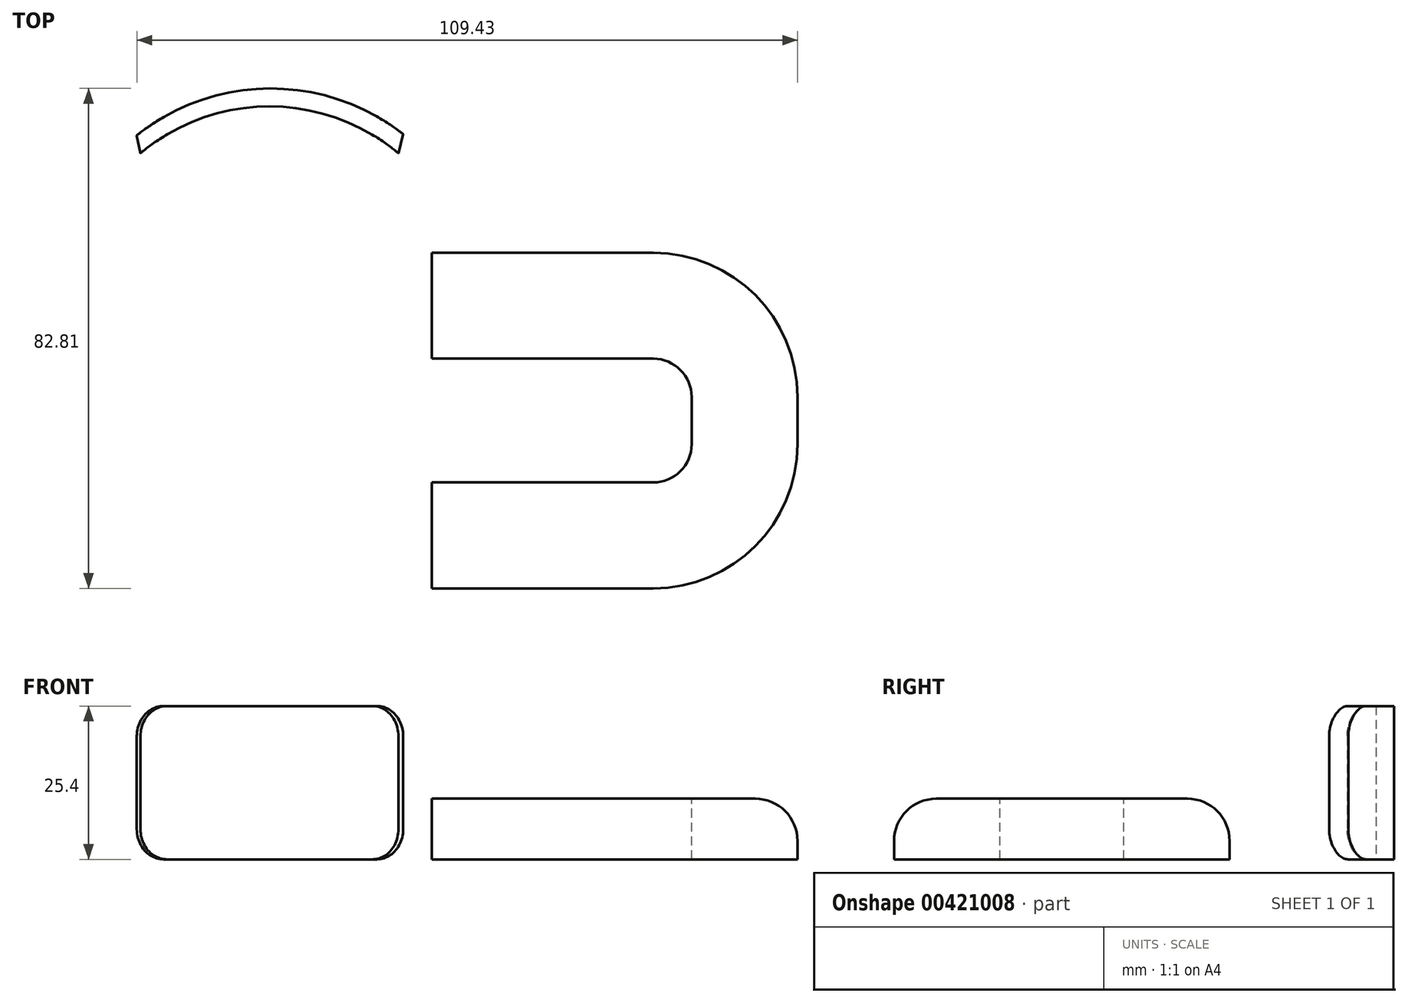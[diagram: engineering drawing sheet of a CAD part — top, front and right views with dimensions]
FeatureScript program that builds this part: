
annotation { "Feature Type Name" : "Feature", "Feature Type Description" : "" }
export const myFeature = defineFeature(function(context is Context, id is Id, definition is map)
    precondition{}
    {
        {
            var Q0;
            Q0=qCreatedBy(makeId("Right.planeOp"),FACE);
            var sketch = newSketch(context, id + "F0", { "sketchPlane" : qUnion([Q0])});
            skLineSegment(sketch, "E0.bottom", {"start": v(0, 0) * mm, "end": v(17.54, 0) * mm});
            skLineSegment(sketch, "E0.top", {"start": v(0, 10.05) * mm, "end": v(10.54, 10.05) * mm});
            skLineSegment(sketch, "E0.left", {"start": v(0, 0) * mm, "end": v(0, 10.05) * mm});
            skLineSegment(sketch, "E0.right", {"start": v(17.54, 0) * mm, "end": v(17.54, 3.05) * mm});
            skPoint(sketch, "E1.visualSharp", {"position": v(17.54, 10.05) * mm});
            skArc(sketch, "E1.filletArc", {"start": v(17.54, 3.05) * mm, "mid": v(15.49, 8) * mm, "end": v(10.54, 10.05) * mm});
            skSolve(sketch);
        }
        {
            var Q0;
            Q0=qCreatedBy(makeId("Top.planeOp"),FACE);
            var sketch = newSketch(context, id + "F1", { "sketchPlane" : qUnion([Q0])});
            skLineSegment(sketch, "E2", {"start": v(0, 0) * mm, "end": v(36.67, 0) * mm});
            skLineSegment(sketch, "E3", {"start": v(43.02, -6.35) * mm, "end": v(43.02, -14.16) * mm});
            skLineSegment(sketch, "E4", {"start": v(36.67, -20.5) * mm, "end": v(0, -20.5) * mm});
            skPoint(sketch, "E5.visualSharp", {"position": v(43.02, 0) * mm});
            skArc(sketch, "E5.filletArc", {"start": v(43.02, -6.35) * mm, "mid": v(41.16, -1.86) * mm, "end": v(36.67, 0) * mm});
            skPoint(sketch, "E6.visualSharp", {"position": v(43.02, -20.5) * mm});
            skArc(sketch, "E6.filletArc", {"start": v(36.67, -20.5) * mm, "mid": v(41.16, -18.65) * mm, "end": v(43.02, -14.16) * mm});
            skSolve(sketch);
        }
        {
            var Q0;
            Q0=makeQuery(id+"F0.imprint","IMPRINT",FACE,{"disambiguationData":[TD([[makeQuery(id+"F0.imprint","IMPRINT",EDGE,{"derivedFrom":sQuery(id+"F0.wireOp",EDGE,"E0.bottom")}),1.0]])]});
            var Q1;
            Q1=sQuery(id+"F1.wireOp",EDGE,"E2");
            var Q2;
            Q2=sQuery(id+"F1.wireOp",EDGE,"E5.filletArc");
            var Q3;
            Q3=sQuery(id+"F1.wireOp",EDGE,"E3");
            var Q4;
            Q4=sQuery(id+"F1.wireOp",EDGE,"E6.filletArc");
            var Q5;
            Q5=sQuery(id+"F1.wireOp",EDGE,"E4");
            sweep(context, id + "F2", {"profiles" : qUnion([Q0]), "path" : qUnion([Q1, Q2, Q3, Q4, Q5])});
        }
        {
            var Q0;
            Q0=qCreatedBy(makeId("Top.planeOp"),FACE);
            var sketch = newSketch(context, id + "F3", { "sketchPlane" : qUnion([Q0])});
            skArc(sketch, "E7", {"start": v(-4.75, 37.2) * mm, "mid": v(-26.84, 44.77) * mm, "end": v(-48.87, 37) * mm});
            skArc(sketch, "E8", {"start": v(-5.54, 34.03) * mm, "mid": v(-26.9, 41.8) * mm, "end": v(-48.28, 34.03) * mm});
            skLineSegment(sketch, "E9", {"start": v(-48.87, 37) * mm, "end": v(-48.28, 34.03) * mm});
            skLineSegment(sketch, "E10", {"start": v(-4.75, 37.2) * mm, "end": v(-5.54, 34.03) * mm});
            skSolve(sketch);
        }
        {
            var Q0;
            Q0=makeQuery(id+"F3.imprint","IMPRINT",FACE,{"disambiguationData":[TD([[makeQuery(id+"F3.imprint","IMPRINT",EDGE,{"derivedFrom":sQuery(id+"F3.wireOp",EDGE,"E7")}),1.0]])]});
            extrude(context, id + "F4", {"entities" : qUnion([Q0]), "depth" : 25.4 * mm});
        }
        {
            var Q0;
            Q0=makeQuery(id+"F4.opExtrude","CAP_EDGE",EDGE,{"disambiguationData":[OSD([sQuery(id+"F3.wireOp",EDGE,"E9")])],"isStart":true});
            fillet(context, id + "F5", {"entities" : qUnion([Q0]), "radius" : 5 * mm, "tangentPropagation" : true, "allowEdgeOverflow" : false});
        }
        {
            var Q0;
            Q0=makeQuery(id+"F4.opExtrude","CAP_EDGE",EDGE,{"disambiguationData":[OSD([sQuery(id+"F3.wireOp",EDGE,"E10")])],"isStart":true});
            fillet(context, id + "F6", {"entities" : qUnion([Q0]), "radius" : 5 * mm, "tangentPropagation" : true, "allowEdgeOverflow" : false});
        }
        {
            var Q0;
            Q0=makeQuery(id+"F4.opExtrude","CAP_EDGE",EDGE,{"disambiguationData":[OSD([sQuery(id+"F3.wireOp",EDGE,"E10")])],"isStart":false});
            fillet(context, id + "F7", {"entities" : qUnion([Q0]), "radius" : 5 * mm, "tangentPropagation" : true, "allowEdgeOverflow" : false});
        }
        {
            var Q0;
            Q0=makeQuery(id+"F4.opExtrude","CAP_EDGE",EDGE,{"disambiguationData":[OSD([sQuery(id+"F3.wireOp",EDGE,"E9")])],"isStart":false});
            fillet(context, id + "F8", {"entities" : qUnion([Q0]), "radius" : 5 * mm, "tangentPropagation" : true, "allowEdgeOverflow" : false});
        }
    });
